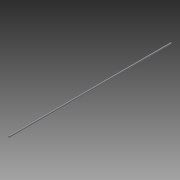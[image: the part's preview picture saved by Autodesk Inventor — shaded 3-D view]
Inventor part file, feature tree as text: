
AUTODESK INVENTOR PART (.ipt)
format: ipt  version: 2014 (Build 180170000, 170)  size: 62,976 bytes
history: native  units: mm
features: other x1, extrude x1, sketch x1
ambient origin geometry x8: Origin, YZ Plane, XZ Plane, XY Plane, X Axis, Y Axis, Z Axis, Center Point
bodies: Body1 (feature_tree)
feature tree (3):
  other  "ソリッド1"
  extrude  "押し出し1"  Depth=3.0mm
  sketch  "スケッチ1"
